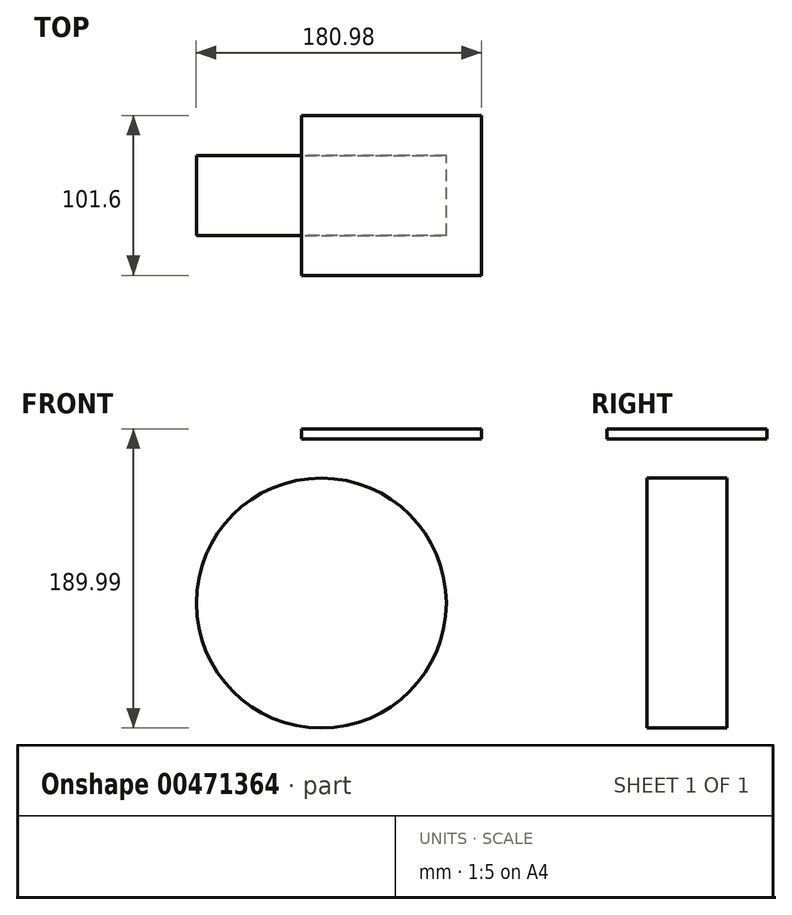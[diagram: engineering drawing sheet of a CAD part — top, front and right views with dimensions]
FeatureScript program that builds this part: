
annotation { "Feature Type Name" : "Feature", "Feature Type Description" : "" }
export const myFeature = defineFeature(function(context is Context, id is Id, definition is map)
    precondition{}
    {
        {
            var Q0;
            Q0=qCreatedBy(makeId("Front.planeOp"),FACE);
            var sketch = newSketch(context, id + "F0", { "sketchPlane" : qUnion([Q0])});
            skCircle(sketch, "E0", {"center": v(-44.45, -110.62) * mm, "radius": 79.38 * mm});
            skSolve(sketch);
        }
        {
            var Q0;
            Q0=makeQuery(id+"F0.imprint","IMPRINT",FACE,{"disambiguationData":[TD([[makeQuery(id+"F0.imprint","IMPRINT",EDGE,{"derivedFrom":sQuery(id+"F0.wireOp",EDGE,"E0")}),1.0]])]});
            extrude(context, id + "F1", {"entities" : qUnion([Q0]), "endBound" : BoundingType.SYMMETRIC, "depth" : 50.8 * mm});
        }
        {
            var Q0;
            Q0=qCreatedBy(makeId("Top.planeOp"),FACE);
            var sketch = newSketch(context, id + "F2", { "sketchPlane" : qUnion([Q0])});
            skLineSegment(sketch, "E1.bottom", {"start": v(57.15, 50.8) * mm, "end": v(-57.15, 50.8) * mm});
            skLineSegment(sketch, "E1.top", {"start": v(57.15, -50.8) * mm, "end": v(-57.15, -50.8) * mm});
            skLineSegment(sketch, "E1.left", {"start": v(57.15, 50.8) * mm, "end": v(57.15, -50.8) * mm});
            skLineSegment(sketch, "E1.right", {"start": v(-57.15, 50.8) * mm, "end": v(-57.15, -50.8) * mm});
            skPoint(sketch, "E1.middle", {"position": v(0, 0) * mm});
            skSolve(sketch);
        }
        {
            var Q0;
            Q0 = qSketchRegion(id + "F2", true);
            extrude(context, id + "F3", {"entities" : qUnion([Q0]), "oppositeDirection" : true, "depth" : 6.35 * mm});
        }
    });
